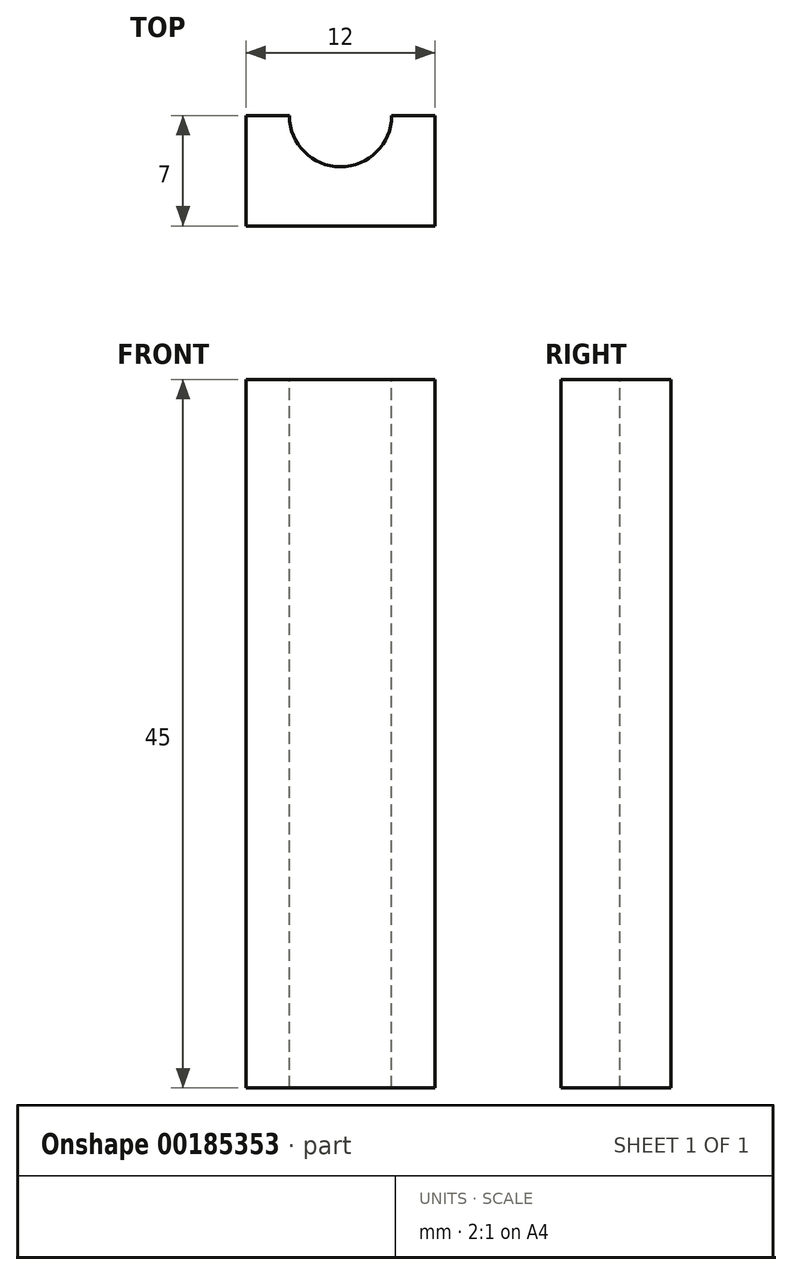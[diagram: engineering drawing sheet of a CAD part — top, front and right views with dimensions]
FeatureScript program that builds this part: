
annotation { "Feature Type Name" : "Feature", "Feature Type Description" : "" }
export const myFeature = defineFeature(function(context is Context, id is Id, definition is map)
    precondition{}
    {
        {
            var Q0;
            Q0=qCreatedBy(makeId("Front.planeOp"),FACE);
            var sketch = newSketch(context, id + "F0", { "sketchPlane" : qUnion([Q0])});
            skLineSegment(sketch, "E0.bottom", {"start": v(6, -22.5) * mm, "end": v(-6, -22.5) * mm});
            skLineSegment(sketch, "E0.top", {"start": v(6, 22.5) * mm, "end": v(-6, 22.5) * mm});
            skLineSegment(sketch, "E0.left", {"start": v(6, -22.5) * mm, "end": v(6, 22.5) * mm});
            skLineSegment(sketch, "E0.right", {"start": v(-6, -22.5) * mm, "end": v(-6, 22.5) * mm});
            skPoint(sketch, "E0.middle", {"position": v(0, 0) * mm});
            skSolve(sketch);
        }
        {
            var Q0;
            Q0 = qSketchRegion(id + "F0", true);
            extrude(context, id + "F1", {"entities" : qUnion([Q0]), "depth" : 7 * mm, "offsetDistance" : 25 * mm});
        }
        {
            var Q0;
            Q0=makeQuery(id+"F1.opExtrude","SWEPT_FACE",FACE,{"disambiguationData":[OSD([sQuery(id+"F0.wireOp",EDGE,"E0.top")])]});
            var sketch = newSketch(context, id + "F2", { "sketchPlane" : qUnion([Q0])});
            skCircle(sketch, "E1", {"center": v(0, 0) * mm, "radius": 3.25 * mm});
            skSolve(sketch);
        }
        {
            var Q0;
            Q0 = qSketchRegion(id + "F2", true);
            extrude(context, id + "F3", {"entities" : qUnion([Q0]), "operationType" : NewBodyOperationType.REMOVE, "endBound" : BoundingType.THROUGH_ALL, "oppositeDirection" : true, "depth" : 25 * mm, "offsetDistance" : 25 * mm});
        }
    });
